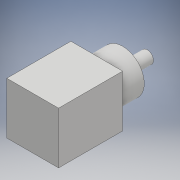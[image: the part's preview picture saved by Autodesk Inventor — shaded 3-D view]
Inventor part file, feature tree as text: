
AUTODESK INVENTOR PART (.ipt)
format: ipt  version: 2018 (Build 220112000, 112)  size: 108,032 bytes
history: native  units: mm
features: extrude x3, sketch x3
ambient origin geometry x8: Origin, YZ Plane, XZ Plane, XY Plane, X Axis, Y Axis, Z Axis, Center Point
bodies: Solid1 (feature_tree)
feature tree (6):
  extrude  "Extrusion1"  Depth=42.0mm
  extrude  "Extrusion2"  Depth=52.0mm
  extrude  "Extrusion3"  Depth=10.0mm
  sketch  "Sketch1"  dims[d0=42.0mm d1=42.0mm]
  sketch  "Sketch2"  dims[d2=52.0mm d3=0.0mm d4=35.0mm]
  sketch  "Sketch3"  dims[d5=21.0mm d6=0.0mm d7=10.0mm d8=10.0mm d9=20.0mm d10=0.0mm]
